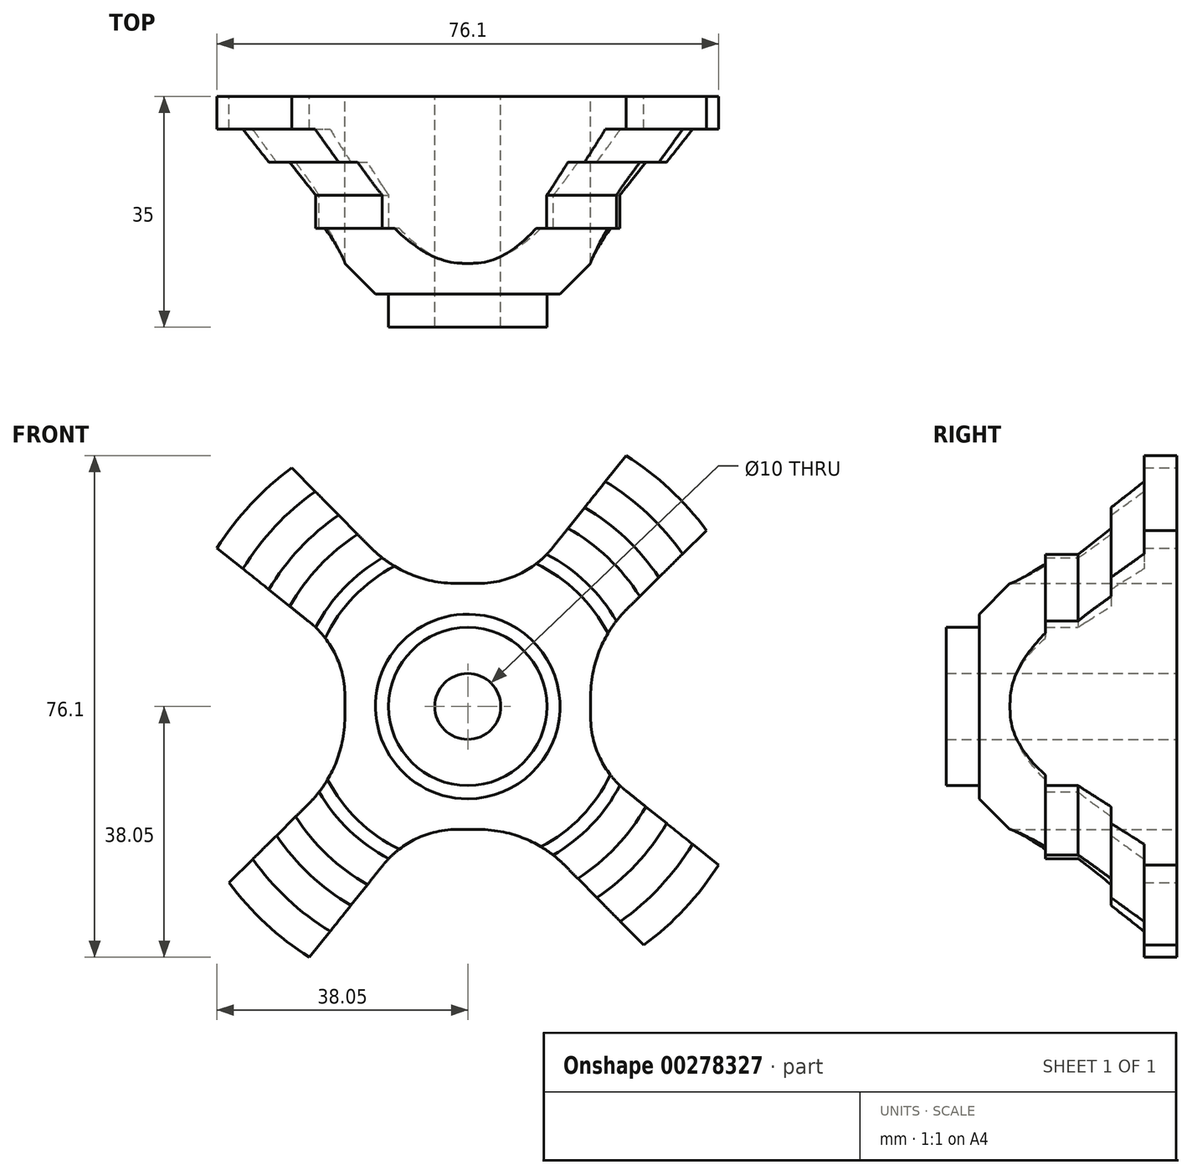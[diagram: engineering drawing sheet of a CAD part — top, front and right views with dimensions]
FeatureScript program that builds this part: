
annotation { "Feature Type Name" : "Feature", "Feature Type Description" : "" }
export const myFeature = defineFeature(function(context is Context, id is Id, definition is map)
    precondition{}
    {
        {
            var Q0;
            Q0=qCreatedBy(makeId("Front.planeOp"),FACE);
            var sketch = newSketch(context, id + "F0", { "sketchPlane" : qUnion([Q0])});
            skCircle(sketch, "E0", {"center": v(0, 0) * mm, "radius": 26 * mm});
            skCircle(sketch, "E1", {"center": v(0, 0) * mm, "radius": 40 * mm});
            skCircle(sketch, "E2", {"center": v(0, 0) * mm, "radius": 19 * mm});
            skCircle(sketch, "E3", {"center": v(0, 0) * mm, "radius": 12 * mm});
            skCircle(sketch, "E4", {"center": v(0, 0) * mm, "radius": 45 * mm});
            skCircle(sketch, "E5", {"center": v(0, 0) * mm, "radius": 5 * mm});
            skSolve(sketch);
        }
        {
            var Q0;
            Q0=makeQuery(id+"F0.imprint","IMPRINT",FACE,{"disambiguationData":[TD([[makeQuery(id+"F0.imprint","IMPRINT",EDGE,{"derivedFrom":sQuery(id+"F0.wireOp",EDGE,"E3")}),1.0]])]});
            extrude(context, id + "F1", {"entities" : qUnion([Q0]), "depth" : 35 * mm});
        }
        {
            var Q0;
            Q0=makeQuery(id+"F0.imprint","IMPRINT",FACE,{"disambiguationData":[TD([[makeQuery(id+"F0.imprint","IMPRINT",EDGE,{"derivedFrom":sQuery(id+"F0.wireOp",EDGE,"E2")}),1.0]])]});
            extrude(context, id + "F2", {"entities" : qUnion([Q0]), "operationType" : NewBodyOperationType.ADD, "depth" : 30 * mm});
        }
        {
            var Q0;
            Q0=makeQuery(id+"F0.imprint","IMPRINT",FACE,{"disambiguationData":[TD([[makeQuery(id+"F0.imprint","IMPRINT",EDGE,{"derivedFrom":sQuery(id+"F0.wireOp",EDGE,"E0")}),1.0]])]});
            extrude(context, id + "F3", {"entities" : qUnion([Q0]), "operationType" : NewBodyOperationType.ADD, "depth" : 20 * mm});
        }
        {
            var Q0;
            Q0=makeQuery(id+"F0.imprint","IMPRINT",FACE,{"disambiguationData":[TD([[makeQuery(id+"F0.imprint","IMPRINT",EDGE,{"derivedFrom":sQuery(id+"F0.wireOp",EDGE,"E0")}),-1.0]])]});
            extrude(context, id + "F4", {"entities" : qUnion([Q0]), "operationType" : NewBodyOperationType.ADD, "depth" : 10 * mm});
        }
        {
            var Q0;
            Q0=makeQuery(id+"F0.imprint","IMPRINT",FACE,{"disambiguationData":[TD([[makeQuery(id+"F0.imprint","IMPRINT",EDGE,{"derivedFrom":sQuery(id+"F0.wireOp",EDGE,"E1")}),-1.0]])]});
            extrude(context, id + "F5", {"entities" : qUnion([Q0]), "operationType" : NewBodyOperationType.ADD, "depth" : 5 * mm});
        }
        {
            var Q0;
            Q0=qCreatedBy(makeId("Right.planeOp"),FACE);
            var sketch = newSketch(context, id + "F6", { "sketchPlane" : qUnion([Q0])});
            skLineSegment(sketch, "E6", {"start": v(-30.03, 18.88) * mm, "end": v(-35.35, 11.7) * mm});
            skLineSegment(sketch, "E7", {"start": v(-29.99, 11.7) * mm, "end": v(-30.03, 18.88) * mm});
            skLineSegment(sketch, "E8", {"start": v(-29.99, 11.7) * mm, "end": v(-35.35, 11.7) * mm});
            skLineSegment(sketch, "E9", {"start": v(-43.25, 0) * mm, "end": v(-26.98, 0) * mm});
            skSolve(sketch);
        }
        {
            var Q0;
            Q0=qCreatedBy(makeId("Right.planeOp"),FACE);
            var sketch = newSketch(context, id + "F7", { "sketchPlane" : qUnion([Q0])});
            skLineSegment(sketch, "E10", {"start": v(-20, 26.03) * mm, "end": v(-25.47, 18.43) * mm});
            skLineSegment(sketch, "E11", {"start": v(-19.98, 18.43) * mm, "end": v(-20, 26.03) * mm});
            skLineSegment(sketch, "E12", {"start": v(-25.47, 18.43) * mm, "end": v(-19.98, 18.43) * mm});
            skLineSegment(sketch, "E13", {"start": v(-45.18, 0) * mm, "end": v(9.5, 0) * mm});
            skSolve(sketch);
        }
        {
            var Q0;
            Q0=qCreatedBy(makeId("Right.planeOp"),FACE);
            var sketch = newSketch(context, id + "F8", { "sketchPlane" : qUnion([Q0])});
            skLineSegment(sketch, "E14", {"start": v(-46.38, 0) * mm, "end": v(4.89, 0) * mm});
            skLineSegment(sketch, "E15", {"start": v(-10.12, 40.05) * mm, "end": v(-15.96, 23.63) * mm});
            skLineSegment(sketch, "E16", {"start": v(-8.69, 23.63) * mm, "end": v(-10.12, 40.05) * mm});
            skLineSegment(sketch, "E17", {"start": v(-8.69, 23.63) * mm, "end": v(-15.96, 23.63) * mm});
            skSolve(sketch);
        }
        {
            var Q0;
            Q0=makeQuery(id+"F4.opExtrude","CAP_FACE",FACE,{"disambiguationData":[OSD([sQuery(id+"F0.wireOp",EDGE,"E0"),sQuery(id+"F0.wireOp",EDGE,"E1")])],"isStart":false});
            chamfer(context, id + "F9", {"entities" : qUnion([Q0]), "width" : 5 * mm, "tangentPropagation" : true});
        }
        {
            var Q0;
            Q0=makeQuery(id+"F0.imprint","IMPRINT",FACE,{"disambiguationData":[TD([[makeQuery(id+"F0.imprint","IMPRINT",EDGE,{"derivedFrom":sQuery(id+"F0.wireOp",EDGE,"E5")}),1.0]])]});
            extrude(context, id + "F10", {"entities" : qUnion([Q0]), "operationType" : NewBodyOperationType.REMOVE, "oppositeDirection" : true, "depth" : 50 * mm});
        }
        {
            var Q0;
            Q0=makeQuery(id+"F2.opExtrude","SWEPT_FACE",FACE,{"disambiguationData":[OSD([sQuery(id+"F0.wireOp",EDGE,"E2")])]});
            chamfer(context, id + "F11", {"entities" : qUnion([Q0]), "width" : 5 * mm, "tangentPropagation" : true});
        }
        {
            var Q0;
            Q0=qCreatedBy(makeId("Front.planeOp"),FACE);
            var sketch = newSketch(context, id + "F12", { "sketchPlane" : qUnion([Q0])});
            skPoint(sketch, "E18.middle", {"position": v(0, 44.71) * mm});
            skLineSegment(sketch, "E19", {"start": v(-38.61, 48.24) * mm, "end": v(-9.33, 18.65) * mm});
            skLineSegment(sketch, "E20", {"start": v(-9.33, 18.65) * mm, "end": v(8.53, 18.65) * mm});
            skLineSegment(sketch, "E21", {"start": v(8.53, 18.65) * mm, "end": v(30.87, 46.6) * mm});
            skLineSegment(sketch, "E22", {"start": v(30.87, 46.6) * mm, "end": v(-38.61, 48.24) * mm});
            skSolve(sketch);
        }
        {
            var Q0;
            Q0 = qSketchRegion(id + "F12", true);
            extrude(context, id + "F13", {"entities" : qUnion([Q0]), "depth" : 50 * mm});
        }
        {
            var Q0;
            Q0=makeQuery(id+"F13.opExtrude","SWEPT_EDGE",EDGE,{"disambiguationData":[OSD([sQuery(id+"F12.wireOp",EDGE,"E19"),sQuery(id+"F12.wireOp",EDGE,"E20")])]});
            fillet(context, id + "F14", {"entities" : qUnion([Q0]), "radius" : 18.51 * mm, "tangentPropagation" : true, "allowEdgeOverflow" : false});
        }
        {
            var Q0;
            Q0=makeQuery(id+"F13.opExtrude","SWEPT_EDGE",EDGE,{"disambiguationData":[OSD([sQuery(id+"F12.wireOp",EDGE,"E20"),sQuery(id+"F12.wireOp",EDGE,"E21")])]});
            fillet(context, id + "F15", {"entities" : qUnion([Q0]), "radius" : 14.4 * mm, "tangentPropagation" : true, "allowEdgeOverflow" : false});
        }
        {
            var Q0;
            Q0=makeQuery(id+"F13.opExtrude","SWEPT_BODY",BODY,{"disambiguationData":[OSD([sQuery(id+"F12.wireOp",EDGE,"E19"),sQuery(id+"F12.wireOp",EDGE,"E20"),sQuery(id+"F12.wireOp",EDGE,"E21"),sQuery(id+"F12.wireOp",EDGE,"E22")])]});
            var Q1;
            Q1=sQuery(id+"F6.wireOp",EDGE,"E9");
            transform(context, id + "F16", {"entities" : qUnion([Q0]), "transformType" : TransformType.ROTATION, "transformAxis" : qUnion([Q1]), "angle" : 90 * degree, "makeCopy" : true});
        }
        {
            var Q0;
            Q0=makeQuery(id+"F13.opExtrude","SWEPT_BODY",BODY,{"disambiguationData":[OSD([sQuery(id+"F12.wireOp",EDGE,"E19"),sQuery(id+"F12.wireOp",EDGE,"E20"),sQuery(id+"F12.wireOp",EDGE,"E21"),sQuery(id+"F12.wireOp",EDGE,"E22")])]});
            var Q1;
            Q1=sQuery(id+"F8.wireOp",EDGE,"E14");
            transform(context, id + "F17", {"entities" : qUnion([Q0]), "transformType" : TransformType.ROTATION, "transformAxis" : qUnion([Q1]), "angle" : 180 * degree, "makeCopy" : true});
        }
        {
            var Q0;
            Q0=makeQuery(id+"F13.opExtrude","SWEPT_BODY",BODY,{"disambiguationData":[OSD([sQuery(id+"F12.wireOp",EDGE,"E19"),sQuery(id+"F12.wireOp",EDGE,"E20"),sQuery(id+"F12.wireOp",EDGE,"E21"),sQuery(id+"F12.wireOp",EDGE,"E22")])]});
            var Q1;
            Q1=sQuery(id+"F7.wireOp",EDGE,"E13");
            transform(context, id + "F18", {"entities" : qUnion([Q0]), "transformType" : TransformType.ROTATION, "transformAxis" : qUnion([Q1]), "angle" : 270 * degree, "makeCopy" : true});
        }
        {
            var Q0;
            Q0=makeQuery(id+"F13.opExtrude","SWEPT_BODY",BODY,{"disambiguationData":[OSD([sQuery(id+"F12.wireOp",EDGE,"E19"),sQuery(id+"F12.wireOp",EDGE,"E20"),sQuery(id+"F12.wireOp",EDGE,"E21"),sQuery(id+"F12.wireOp",EDGE,"E22")])]});
            var Q1;
            Q1=makeQuery(id+"F1.opExtrude","SWEPT_BODY",BODY,{"disambiguationData":[OSD([sQuery(id+"F0.wireOp",EDGE,"E3"),sQuery(id+"F0.wireOp",EDGE,"E5")])]});
            booleanBodies(context, id + "F19", {"operationType" : BooleanOperationType.SUBTRACTION, "tools" : qUnion([Q0]), "targets" : qUnion([Q1])});
        }
        {
            var Q0;
            Q0=makeQuery(id+"F17.opPattern","COPY",BODY,{"derivedFrom":makeQuery(id+"F13.opExtrude","SWEPT_BODY",BODY,{"disambiguationData":[OSD([sQuery(id+"F12.wireOp",EDGE,"E19"),sQuery(id+"F12.wireOp",EDGE,"E20"),sQuery(id+"F12.wireOp",EDGE,"E21"),sQuery(id+"F12.wireOp",EDGE,"E22")])]}),"instanceName":"1"});
            var Q1;
            Q1=makeQuery(id+"F1.opExtrude","SWEPT_BODY",BODY,{"disambiguationData":[OSD([sQuery(id+"F0.wireOp",EDGE,"E3"),sQuery(id+"F0.wireOp",EDGE,"E5")])]});
            booleanBodies(context, id + "F20", {"operationType" : BooleanOperationType.SUBTRACTION, "tools" : qUnion([Q0]), "targets" : qUnion([Q1])});
        }
        {
            var Q0;
            Q0=makeQuery(id+"F16.opPattern","COPY",BODY,{"derivedFrom":makeQuery(id+"F13.opExtrude","SWEPT_BODY",BODY,{"disambiguationData":[OSD([sQuery(id+"F12.wireOp",EDGE,"E19"),sQuery(id+"F12.wireOp",EDGE,"E20"),sQuery(id+"F12.wireOp",EDGE,"E21"),sQuery(id+"F12.wireOp",EDGE,"E22")])]}),"instanceName":"1"});
            var Q1;
            Q1=makeQuery(id+"F1.opExtrude","SWEPT_BODY",BODY,{"disambiguationData":[OSD([sQuery(id+"F0.wireOp",EDGE,"E3"),sQuery(id+"F0.wireOp",EDGE,"E5")])]});
            booleanBodies(context, id + "F21", {"operationType" : BooleanOperationType.SUBTRACTION, "tools" : qUnion([Q0]), "targets" : qUnion([Q1])});
        }
        {
            var Q0;
            Q0=makeQuery(id+"F18.opPattern","COPY",BODY,{"derivedFrom":makeQuery(id+"F13.opExtrude","SWEPT_BODY",BODY,{"disambiguationData":[OSD([sQuery(id+"F12.wireOp",EDGE,"E19"),sQuery(id+"F12.wireOp",EDGE,"E20"),sQuery(id+"F12.wireOp",EDGE,"E21"),sQuery(id+"F12.wireOp",EDGE,"E22")])]}),"instanceName":"1"});
            var Q1;
            Q1=makeQuery(id+"F1.opExtrude","SWEPT_BODY",BODY,{"disambiguationData":[OSD([sQuery(id+"F0.wireOp",EDGE,"E3"),sQuery(id+"F0.wireOp",EDGE,"E5")])]});
            booleanBodies(context, id + "F22", {"operationType" : BooleanOperationType.SUBTRACTION, "tools" : qUnion([Q0]), "targets" : qUnion([Q1])});
        }
    });
